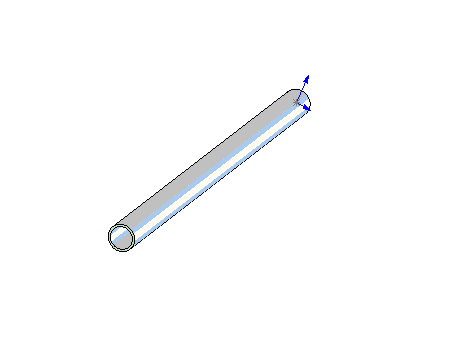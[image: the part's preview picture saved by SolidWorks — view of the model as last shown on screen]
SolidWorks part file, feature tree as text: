
SOLIDWORKS PART (.sldprt)
format: sldprt  version: not decoded by parser v0  size: 111,616 bytes
history: native  units: mm
features: plane x3, sketch x3, material x1, extrude x1, hole x1, thread x1 + 1 further entry (+7 scaffold rows collapsed)
feature tree (18):
  scaffold x7  (default folders/planes/origin — collapsed)
  material  "Matériau <non spécifié>"
  "Corps de surface"
  plane  "Face"
  plane  "Dessus"
  plane  "Droite"
  sketch  "Esquisse1"  dims[D1=18.0mm D2=15.0mm]
  extrude  "Extrusion1"  Depth=305mm
  hole  "Trou taraudé M16x2.01"  Diameter=14mm Depth=305mm
  sketch  "Esquisse5"
  sketch  "Esquisse6"  dims[hole-wizard template sketch: 59 standard entries collapsed; hole parameters kept: c18.Diamètre du trou pour taraudage jusqu'au prochain=14.0mm c18.Profondeur du trou pour taraudage jusqu'au prochain=305.0mm]
  thread  "Représentation de filetage1"  Diameter=32mm  [1 undecoded]
decode coverage: 5 of 6 modeling features carry decoded parameters; 1 rows unclassified (native names shown)
note: ~ marks probable driven/reference dimensions
note: 1 parameter value undecoded
note: suppression state not decoded; provenance and decode notes live in map.json
